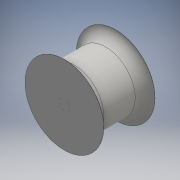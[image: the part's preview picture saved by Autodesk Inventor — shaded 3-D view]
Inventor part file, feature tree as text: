
AUTODESK INVENTOR PART (.ipt)
format: ipt  version: 2016 (Build 200138000, 138)  size: 155,136 bytes
history: native  units: mm
features: extrude x4, sketch x4, fillet x2
ambient origin geometry x8: Origin, YZ Plane, XZ Plane, XY Plane, X Axis, Y Axis, Z Axis, Center Point
bodies: Solid1 (feature_tree)
feature tree (10):
  extrude  "Extrusion1"  Depth=26.0mm TaperAngle=0.0deg
  extrude  "Extrusion2"  Depth=26.0mm TaperAngle=0.0deg
  extrude  "Extrusion3"  Depth=0.1mm TaperAngle=0.0deg
  fillet  "Fillet1"  Radius=5.0mm
  extrude  "Extrusion4"  Depth=0.1mm TaperAngle=0.0deg
  fillet  "Fillet2"  Radius=5.0mm
  sketch  "Sketch1"  dims[d0=30.0mm d1=26.0mm d2=0.0mm]
  sketch  "Sketch2"  dims[d3=5.5mm d4=26.0mm d5=0.0mm]
  sketch  "Sketch3"  dims[d6=40.0mm d7=0.1mm d8=0.0mm d9=5.0mm]
  sketch  "Sketch4"  dims[d10=40.0mm d11=0.1mm d12=0.0mm d13=5.0mm]
